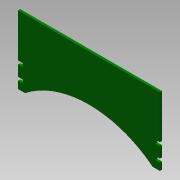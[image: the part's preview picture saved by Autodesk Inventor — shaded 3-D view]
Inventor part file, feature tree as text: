
AUTODESK INVENTOR PART (.ipt)
format: ipt  version: 2015 (Build 190159000, 159)  size: 122,880 bytes
history: native  units: in
note: dims shown in document units (in); Inventor stores cm internally (conversion verified against a paired STEP export)
features: extrude x1, sketch x1
ambient origin geometry x8: Origin, YZ Plane, XZ Plane, XY Plane, X Axis, Y Axis, Z Axis, Center Point
bodies: Body1 (feature_tree)
feature tree (2):
  extrude  "Extrusion4"  Depth=0.3937in
  sketch  "Sketch2"  dims[d0=2.874in d4=0.315in d33=3.937in d34=8.3071in d35=0.0618in d36=0.0in d37=4.5276in d38=0.0984in d39=0.0984in d40=0.128in d41=0.0098in d42=0.128in d43=0.1969in d44=0.3937in]
